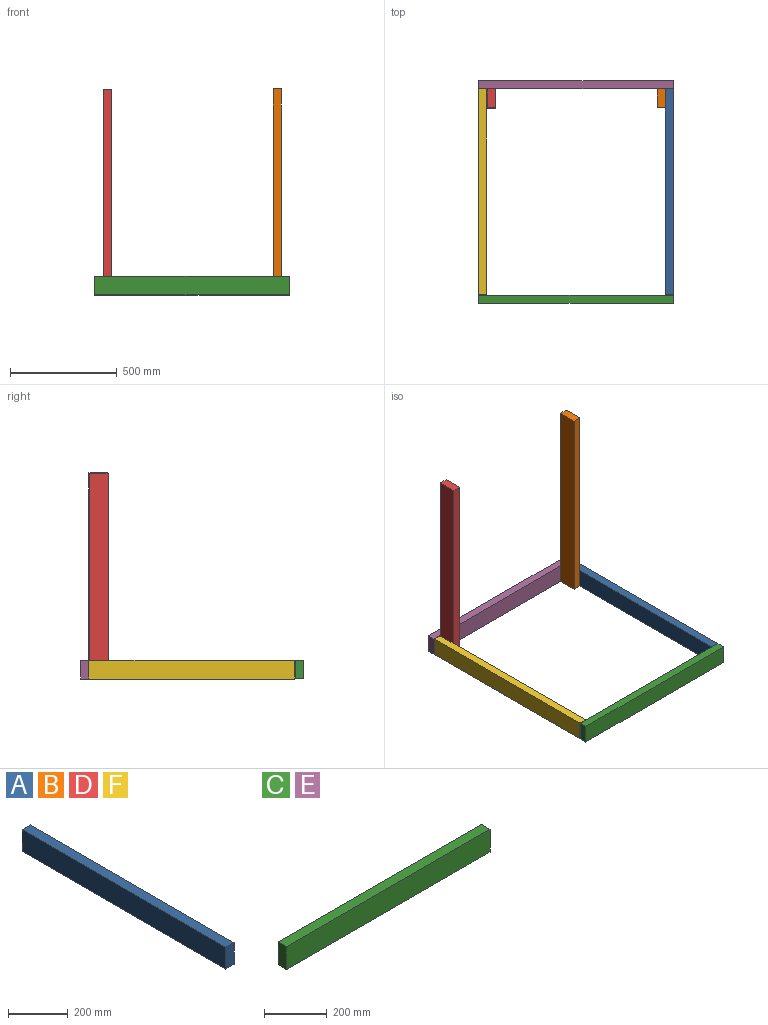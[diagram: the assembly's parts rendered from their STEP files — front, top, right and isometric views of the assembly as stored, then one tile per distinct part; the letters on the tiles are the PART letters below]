
ASSEMBLY  parts=6 mates=2
PART A: 6 faces, bbox 38.1x965.2x88.9 mm
  f0: plane 965.2x38.1mm, normal (0,0,1), area 36774.1mm2, adj f1,f3,f4,f5
  f1: plane 965.2x88.9mm, normal (-1,0,0), area 85806.3mm2, adj f0,f2,f4,f5
  f2: plane 965.2x38.1mm, normal (0,0,-1), area 36774.1mm2, adj f1,f3,f4,f5
  f3: plane 965.2x88.9mm, normal (1,0,0), area 85806.3mm2, adj f0,f2,f4,f5
  f4: plane 88.9x38.1mm, normal (0,-1,0), area 3387.1mm2, adj f0,f1,f2,f3
  f5: plane 88.9x38.1mm, normal (0,1,0), area 3387.1mm2, adj f0,f1,f2,f3
PART B: same geometry as A
PART C: 6 faces, bbox 914.4x38.1x88.9 mm
  f0: plane 914.4x38.1mm, normal (0,0,1), area 34838.6mm2, adj f1,f3,f4,f5
  f1: plane 914.4x88.9mm, normal (0,-1,0), area 81290.2mm2, adj f0,f2,f4,f5
  f2: plane 914.4x38.1mm, normal (0,0,-1), area 34838.6mm2, adj f1,f3,f4,f5
  f3: plane 914.4x88.9mm, normal (0,1,0), area 81290.2mm2, adj f0,f2,f4,f5
  f4: plane 88.9x38.1mm, normal (1,0,0), area 3387.1mm2, adj f0,f1,f2,f3
  f5: plane 88.9x38.1mm, normal (-1,0,0), area 3387.1mm2, adj f0,f1,f2,f3
PART D: same geometry as A
PART E: same geometry as C
PART F: same geometry as A
PLACE A t=(627.02,497.92,-167.76)mm
PLACE B rot(axis=(1,0,0),90deg) t=(588.94,499.72,800.81)mm
PLACE C t=(-323.67,-411.98,-177.33)mm
PLACE D rot(axis=(1,0,0),90deg) t=(-208.33,499.08,800.03)mm
PLACE E t=(-323.99,593.86,-177.7)mm
PLACE F t=(-248.44,498.44,-167.94)mm
MATE parallel F.f3 <-> E.f5  axis (1,0,0) through (-284.98,15.84,-121.37)mm
MATE parallel E.f1 <-> F.f5  axis (0,-1,0) through (133.21,498.44,-121.37)mm
